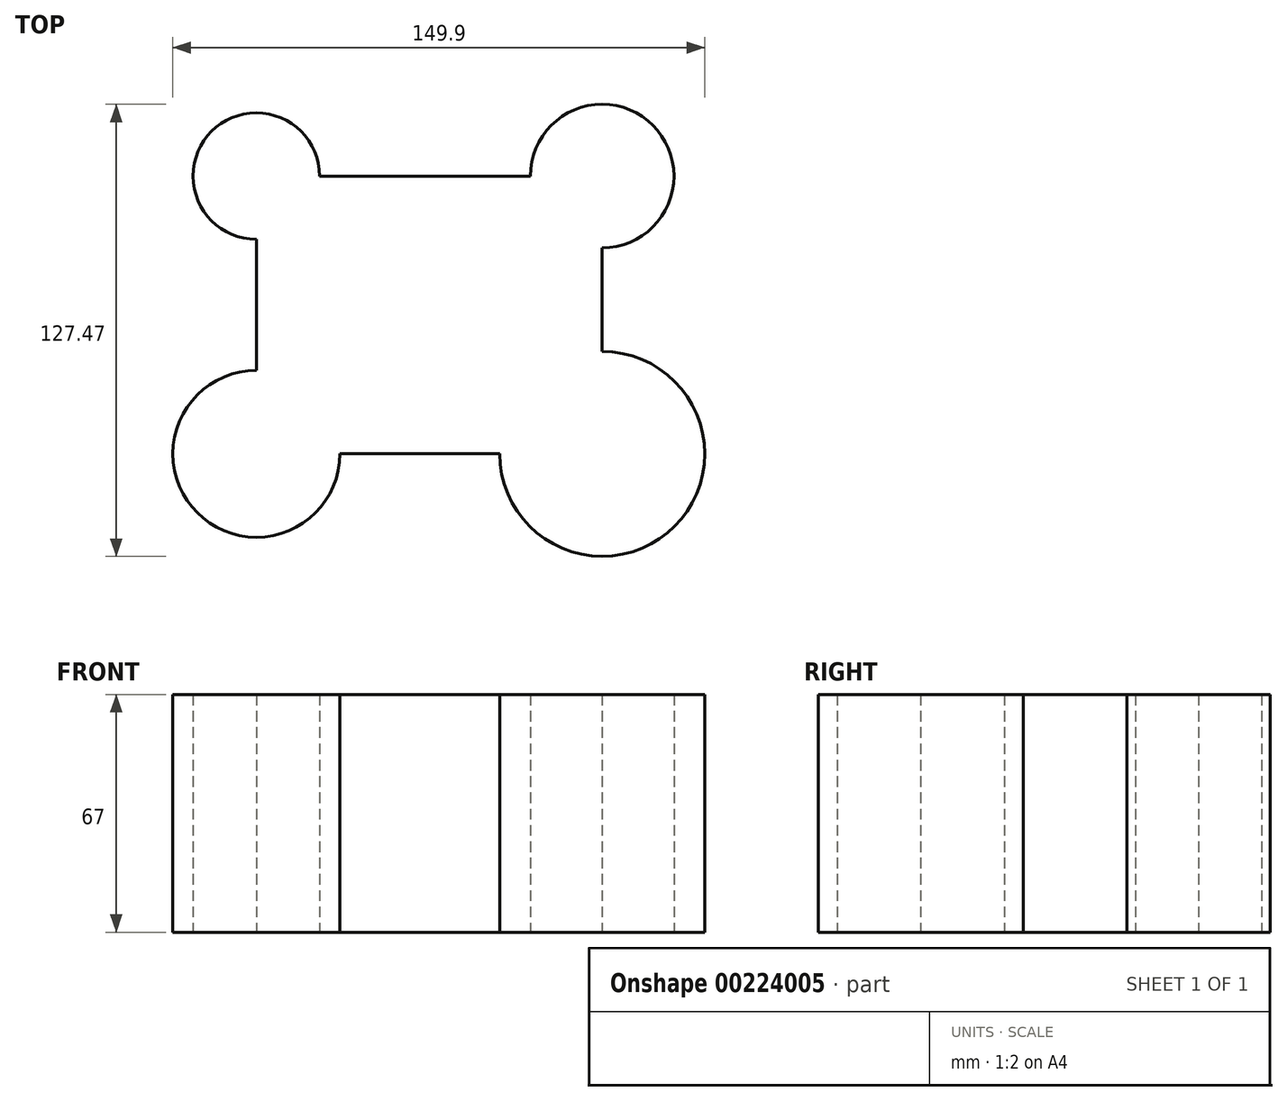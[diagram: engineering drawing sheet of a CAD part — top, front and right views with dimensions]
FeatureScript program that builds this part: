
annotation { "Feature Type Name" : "Feature", "Feature Type Description" : "" }
export const myFeature = defineFeature(function(context is Context, id is Id, definition is map)
    precondition{}
    {
        {
            var Q0;
            Q0=qCreatedBy(makeId("Top.planeOp"),FACE);
            var sketch = newSketch(context, id + "F0", { "sketchPlane" : qUnion([Q0])});
            skLineSegment(sketch, "E0.bottom", {"start": v(-26.44, 45.42) * mm, "end": v(32.95, 45.42) * mm});
            skLineSegment(sketch, "E0.top", {"start": v(-20.75, -32.9) * mm, "end": v(24.3, -32.9) * mm});
            skLineSegment(sketch, "E0.left", {"start": v(-44.28, 27.58) * mm, "end": v(-44.28, -9.38) * mm});
            skLineSegment(sketch, "E0.right", {"start": v(53.2, 25.16) * mm, "end": v(53.2, -4) * mm});
            skArc(sketch, "E1", {"start": v(53.2, 25.16) * mm, "mid": v(67.52, 59.74) * mm, "end": v(32.95, 45.42) * mm});
            skArc(sketch, "E2", {"start": v(24.3, -32.9) * mm, "mid": v(73.63, -53.34) * mm, "end": v(53.2, -4) * mm});
            skArc(sketch, "E3", {"start": v(-44.28, -9.38) * mm, "mid": v(-60.91, -49.54) * mm, "end": v(-20.75, -32.9) * mm});
            skArc(sketch, "E4", {"start": v(-26.44, 45.42) * mm, "mid": v(-56.9, 58.03) * mm, "end": v(-44.28, 27.58) * mm});
            skSolve(sketch);
        }
        {
            var Q0;
            Q0=makeQuery(id+"F0.imprint","IMPRINT",FACE,{"disambiguationData":[TD([[makeQuery(id+"F0.imprint","IMPRINT",EDGE,{"derivedFrom":sQuery(id+"F0.wireOp",EDGE,"E0.bottom")}),-1.0]])]});
            extrude(context, id + "F1", {"entities" : qUnion([Q0]), "depth" : 67 * mm});
        }
    });
